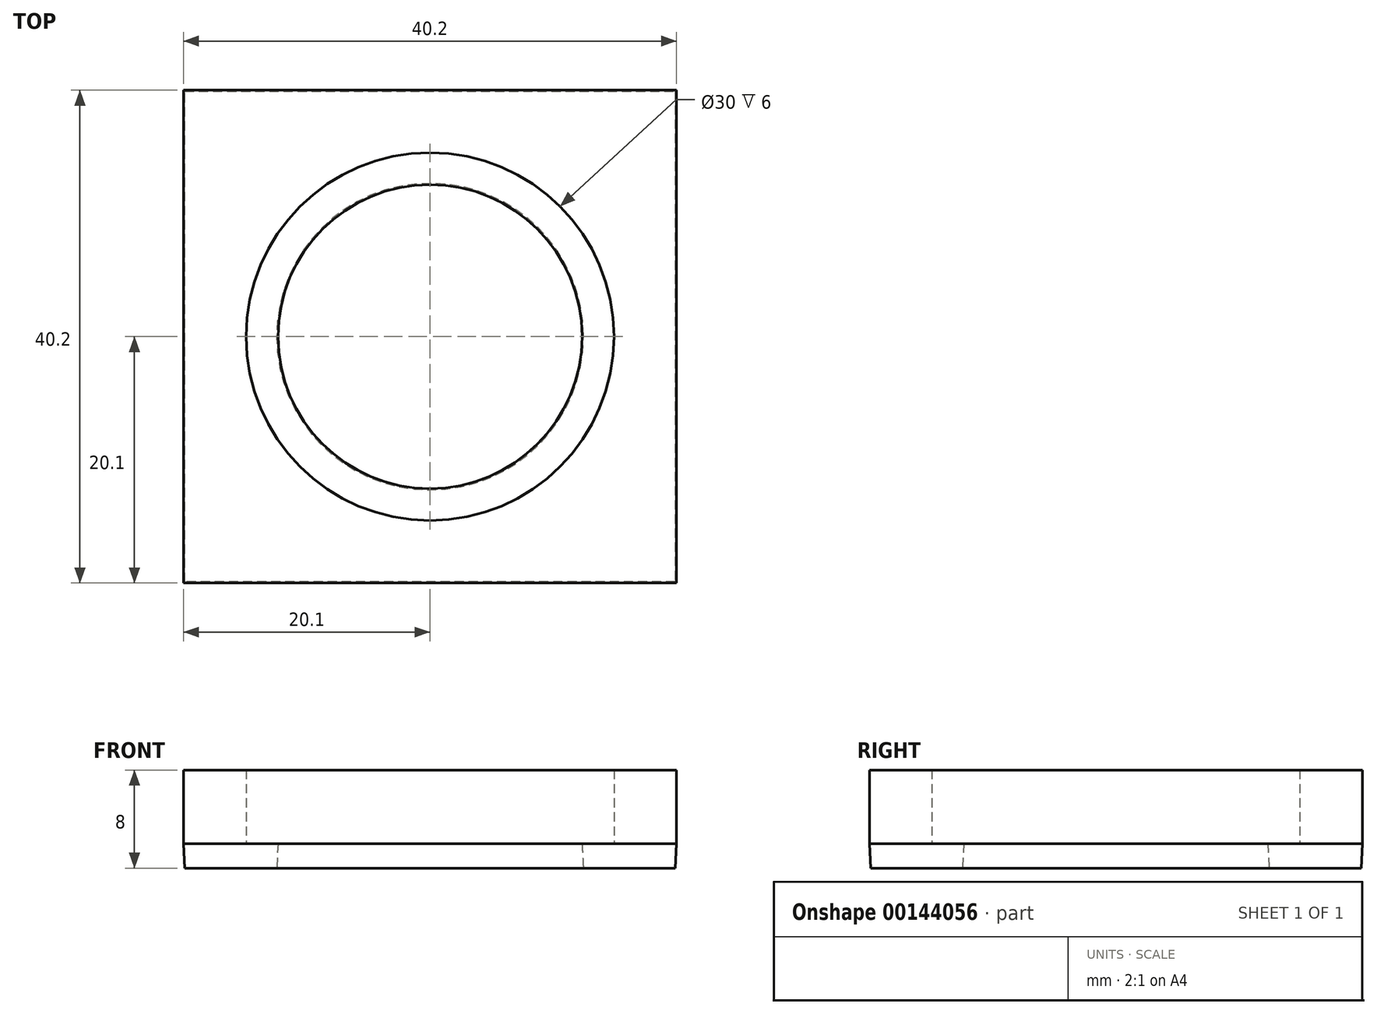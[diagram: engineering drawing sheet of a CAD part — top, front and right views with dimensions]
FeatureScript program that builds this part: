
annotation { "Feature Type Name" : "Feature", "Feature Type Description" : "" }
export const myFeature = defineFeature(function(context is Context, id is Id, definition is map)
    precondition{}
    {
        {
            var Q0;
            Q0=qCreatedBy(makeId("Top.planeOp"),FACE);
            var sketch = newSketch(context, id + "F0", { "sketchPlane" : qUnion([Q0])});
            skCircle(sketch, "E0", {"center": v(0, 0) * mm, "radius": 12.5 * mm});
            skLineSegment(sketch, "E1.bottom", {"start": v(20, 20) * mm, "end": v(-20, 20) * mm});
            skLineSegment(sketch, "E1.top", {"start": v(20, -20) * mm, "end": v(-20, -20) * mm});
            skLineSegment(sketch, "E1.left", {"start": v(20, 20) * mm, "end": v(20, -20) * mm});
            skLineSegment(sketch, "E1.right", {"start": v(-20, 20) * mm, "end": v(-20, -20) * mm});
            skSolve(sketch);
        }
        {
            var Q0;
            Q0=makeQuery(id+"F0.imprint","IMPRINT",FACE,{"disambiguationData":[TD([[makeQuery(id+"F0.imprint","IMPRINT",EDGE,{"derivedFrom":sQuery(id+"F0.wireOp",EDGE,"E0")}),-1.0]])]});
            extrude(context, id + "F1", {"entities" : qUnion([Q0]), "depth" : 2 * mm, "hasDraft" : true, "draftAngle" : 3 * degree});
        }
        {
            var Q0;
            Q0=makeQuery(id+"F1.opExtrude","CAP_FACE",FACE,{"disambiguationData":[OSD([sQuery(id+"F0.wireOp",EDGE,"E0"),sQuery(id+"F0.wireOp",EDGE,"E1.bottom"),sQuery(id+"F0.wireOp",EDGE,"E1.top"),sQuery(id+"F0.wireOp",EDGE,"E1.left"),sQuery(id+"F0.wireOp",EDGE,"E1.right")])],"isStart":false});
            var sketch = newSketch(context, id + "F2", { "sketchPlane" : qUnion([Q0])});
            skCircle(sketch, "E2", {"center": v(0, 0) * mm, "radius": 15 * mm});
            skLineSegment(sketch, "E3.bottom", {"start": v(20.1, 20.1) * mm, "end": v(-20.1, 20.1) * mm});
            skLineSegment(sketch, "E3.top", {"start": v(20.1, -20.1) * mm, "end": v(-20.1, -20.1) * mm});
            skLineSegment(sketch, "E3.left", {"start": v(20.1, 20.1) * mm, "end": v(20.1, -20.1) * mm});
            skLineSegment(sketch, "E3.right", {"start": v(-20.1, 20.1) * mm, "end": v(-20.1, -20.1) * mm});
            skSolve(sketch);
        }
        {
            var Q0;
            Q0=makeQuery(id+"F2.imprint","IMPRINT",FACE,{"disambiguationData":[TD([[makeQuery(id+"F2.imprint","IMPRINT",EDGE,{"derivedFrom":sQuery(id+"F2.wireOp",EDGE,"E2")}),-1.0]])]});
            extrude(context, id + "F3", {"entities" : qUnion([Q0]), "operationType" : NewBodyOperationType.ADD, "depth" : 6 * mm});
        }
    });
